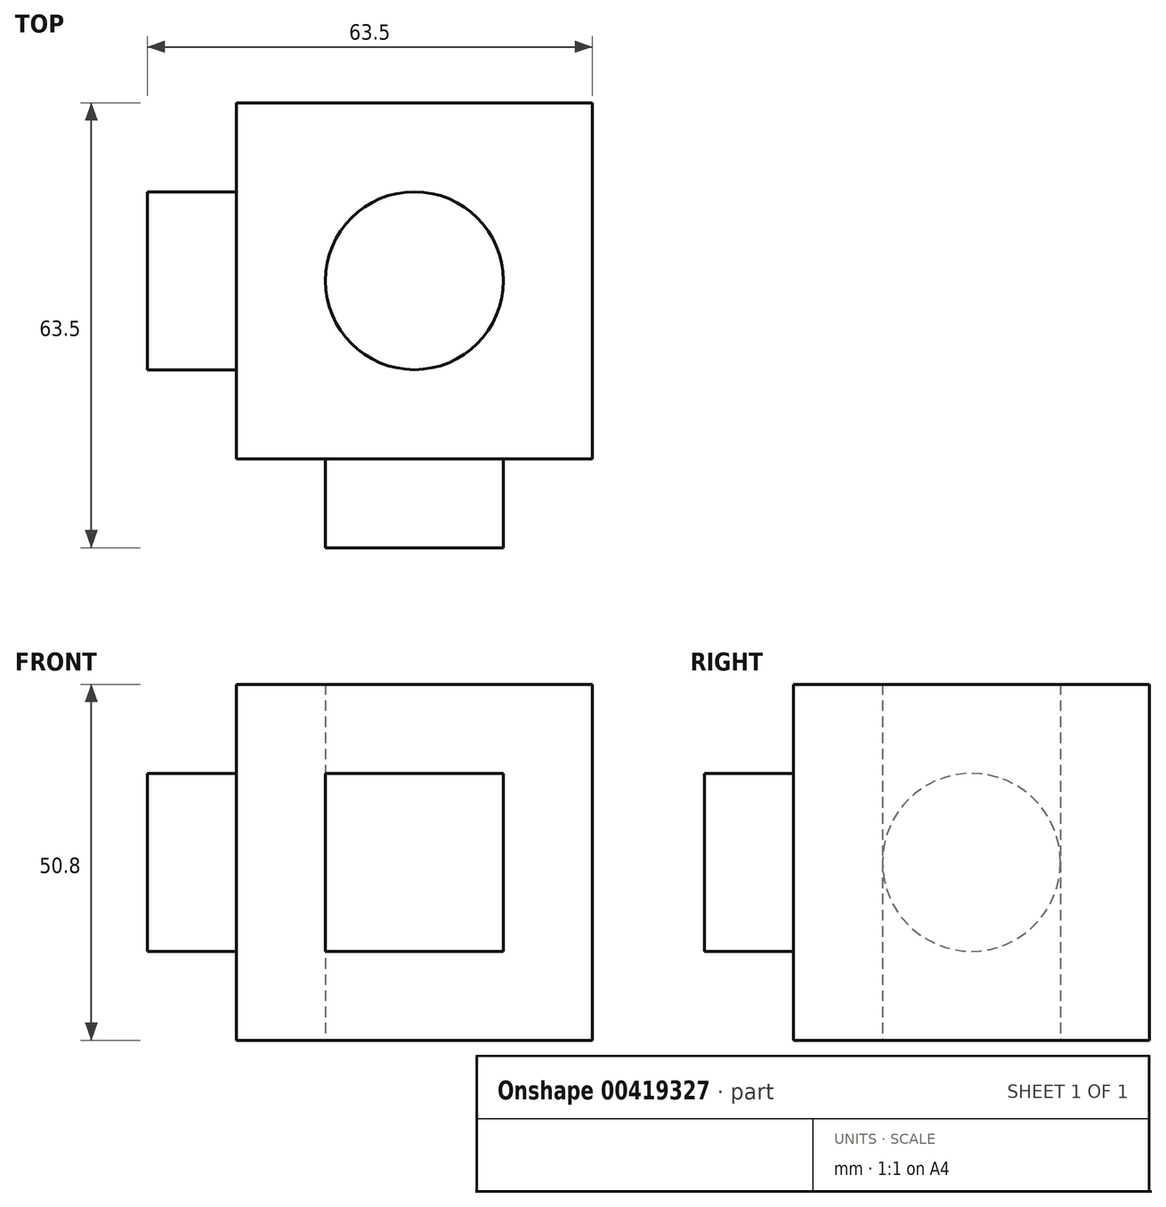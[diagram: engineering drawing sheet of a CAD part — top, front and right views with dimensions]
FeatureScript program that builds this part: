
annotation { "Feature Type Name" : "Feature", "Feature Type Description" : "" }
export const myFeature = defineFeature(function(context is Context, id is Id, definition is map)
    precondition{}
    {
        {
            var Q0;
            Q0=qCreatedBy(makeId("Front.planeOp"),FACE);
            var sketch = newSketch(context, id + "F0", { "sketchPlane" : qUnion([Q0])});
            skLineSegment(sketch, "E0", {"start": v(0, 0) * mm, "end": v(0, 50.8) * mm});
            skLineSegment(sketch, "E1", {"start": v(0, 50.8) * mm, "end": v(50.8, 50.8) * mm});
            skLineSegment(sketch, "E2", {"start": v(50.8, 50.8) * mm, "end": v(50.8, 0) * mm});
            skLineSegment(sketch, "E3", {"start": v(50.8, 0) * mm, "end": v(0, 0) * mm});
            skSolve(sketch);
        }
        {
            var Q0;
            Q0=makeQuery(id+"F0.imprint","IMPRINT",FACE,{"disambiguationData":[TD([[makeQuery(id+"F0.imprint","IMPRINT",EDGE,{"derivedFrom":sQuery(id+"F0.wireOp",EDGE,"E0")}),-1.0]])]});
            extrude(context, id + "F1", {"entities" : qUnion([Q0]), "depth" : 50.8 * mm});
        }
        {
            var Q0;
            Q0=makeQuery(id+"F1.opExtrude","SWEPT_FACE",FACE,{"disambiguationData":[OSD([sQuery(id+"F0.wireOp",EDGE,"E3")])]});
            var sketch = newSketch(context, id + "F2", { "sketchPlane" : qUnion([Q0])});
            skCircle(sketch, "E4", {"center": v(25.4, 25.4) * mm, "radius": 12.7 * mm});
            skSolve(sketch);
        }
        {
            var Q0;
            Q0=makeQuery(id+"F2.imprint","IMPRINT",FACE,{"disambiguationData":[TD([[makeQuery(id+"F2.imprint","IMPRINT",EDGE,{"derivedFrom":sQuery(id+"F2.wireOp",EDGE,"E4")}),1.0]])]});
            extrude(context, id + "F3", {"entities" : qUnion([Q0]), "operationType" : NewBodyOperationType.REMOVE, "oppositeDirection" : true, "depth" : 50.8 * mm});
        }
        {
            var Q0;
            Q0=makeQuery(id+"F1.opExtrude","CAP_FACE",FACE,{"disambiguationData":[OSD([sQuery(id+"F0.wireOp",EDGE,"E0"),sQuery(id+"F0.wireOp",EDGE,"E1"),sQuery(id+"F0.wireOp",EDGE,"E2"),sQuery(id+"F0.wireOp",EDGE,"E3")])],"isStart":false});
            var sketch = newSketch(context, id + "F4", { "sketchPlane" : qUnion([Q0])});
            skLineSegment(sketch, "E5", {"start": v(38.1, 12.7) * mm, "end": v(38.1, 38.1) * mm});
            skLineSegment(sketch, "E6", {"start": v(38.1, 12.7) * mm, "end": v(12.7, 12.7) * mm});
            skLineSegment(sketch, "E7", {"start": v(12.7, 12.7) * mm, "end": v(12.7, 38.1) * mm});
            skLineSegment(sketch, "E8", {"start": v(12.7, 38.1) * mm, "end": v(38.1, 38.1) * mm});
            skSolve(sketch);
        }
        {
            var Q0;
            Q0=makeQuery(id+"F4.imprint","IMPRINT",FACE,{"disambiguationData":[TD([[makeQuery(id+"F4.imprint","IMPRINT",EDGE,{"derivedFrom":sQuery(id+"F4.wireOp",EDGE,"E5")}),1.0]])]});
            extrude(context, id + "F5", {"entities" : qUnion([Q0]), "operationType" : NewBodyOperationType.ADD, "depth" : 12.7 * mm});
        }
        {
            var Q0;
            Q0=makeQuery(id+"F1.opExtrude","SWEPT_FACE",FACE,{"disambiguationData":[OSD([sQuery(id+"F0.wireOp",EDGE,"E0")])]});
            var sketch = newSketch(context, id + "F6", { "sketchPlane" : qUnion([Q0])});
            skCircle(sketch, "E9", {"center": v(25.4, 25.4) * mm, "radius": 12.7 * mm});
            skSolve(sketch);
        }
        {
            var Q0;
            Q0=makeQuery(id+"F6.imprint","IMPRINT",FACE,{"disambiguationData":[TD([[makeQuery(id+"F6.imprint","IMPRINT",EDGE,{"derivedFrom":sQuery(id+"F6.wireOp",EDGE,"E9")}),1.0]])]});
            extrude(context, id + "F7", {"entities" : qUnion([Q0]), "operationType" : NewBodyOperationType.ADD, "depth" : 12.7 * mm});
        }
    });
